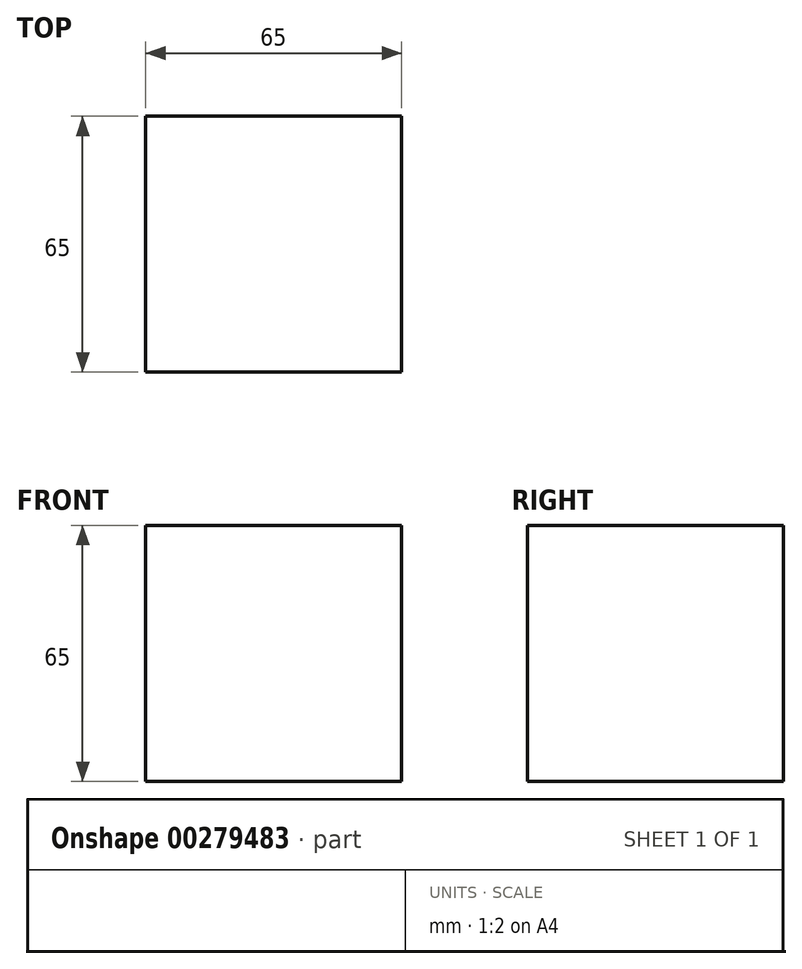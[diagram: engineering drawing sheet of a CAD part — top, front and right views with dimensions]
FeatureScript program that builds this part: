
annotation { "Feature Type Name" : "Feature", "Feature Type Description" : "" }
export const myFeature = defineFeature(function(context is Context, id is Id, definition is map)
    precondition{}
    {
        {
            var Q0;
            Q0=qCreatedBy(makeId("Top.planeOp"),FACE);
            var sketch = newSketch(context, id + "F0", { "sketchPlane" : qUnion([Q0])});
            skLineSegment(sketch, "E0", {"start": v(0, 0) * mm, "end": v(0, 65) * mm});
            skLineSegment(sketch, "E1", {"start": v(0, 65) * mm, "end": v(65, 65) * mm});
            skLineSegment(sketch, "E2", {"start": v(65, 65) * mm, "end": v(65, 0) * mm});
            skLineSegment(sketch, "E3", {"start": v(65, 0) * mm, "end": v(0, 0) * mm});
            skSolve(sketch);
        }
        {
            var Q0;
            Q0 = qSketchRegion(id + "F0", true);
            extrude(context, id + "F1", {"entities" : qUnion([Q0]), "depth" : 65 * mm});
        }
    });
